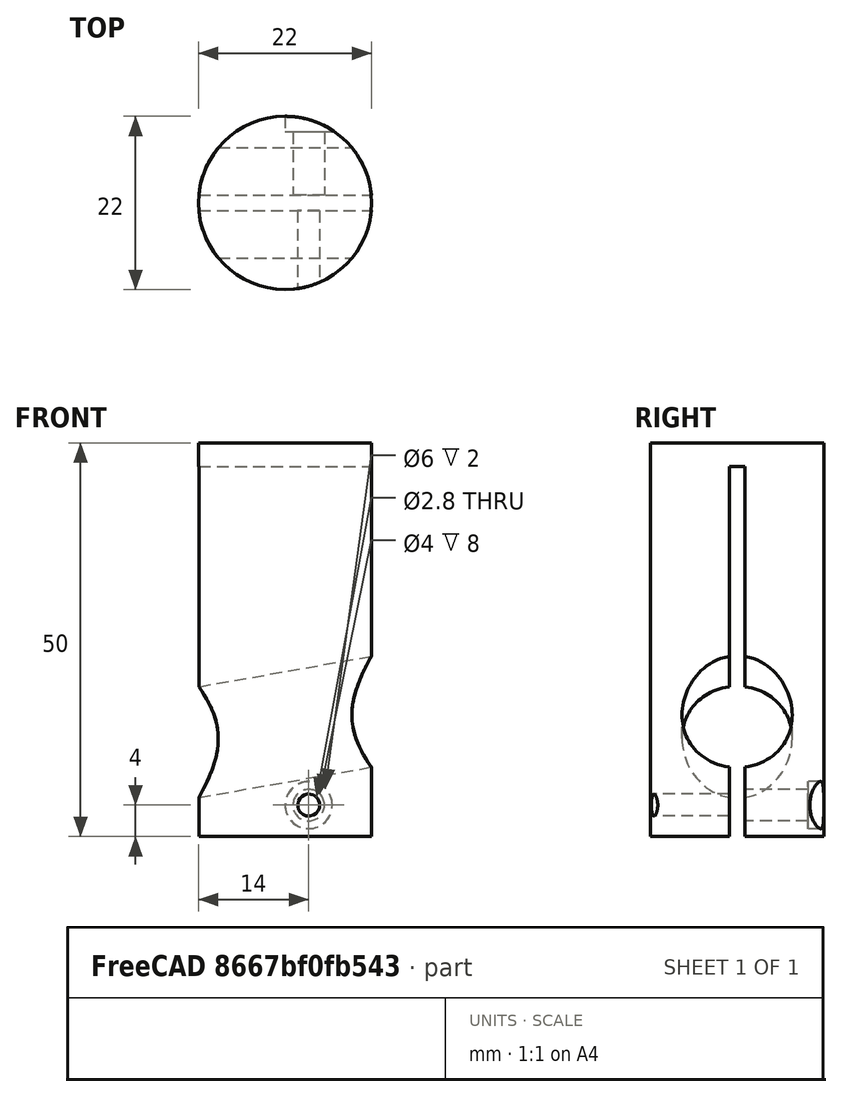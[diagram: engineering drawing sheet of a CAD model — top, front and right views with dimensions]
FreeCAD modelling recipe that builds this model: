
FCSTD DOCUMENT  (FreeCAD 0.19R)
Label: 14mmSSMount
License: All rights reserved
LicenseURL: http://en.wikipedia.org/wiki/All_rights_reserved
objects: Part::Cylinder×5, Part::Cut×5, PartDesign::Body×1, Part::Box×1
note: 12 computed .brp shape members not serialized (recipe doc carries the construction recipe); baked Part::Feature solids carry a one-line shape summary decoded from their .brp

FEATURE [PartDesign::Body] Body
  Origin = -> Origin
FEATURE [Part::Cylinder] Cylinder
  Angle = 360
  AttacherType = Attacher::AttachEngine3D
  Height = 50
  Radius = 11
FEATURE [Part::Cylinder] Cylinder001
  Angle = 360
  AttacherType = Attacher::AttachEngine3D
  Height = 100
  Placement = pos=(-28,0,9) rot=(0,1,0;1.39626rad)
  Radius = 7
FEATURE [Part::Cut] Cut
  Base = -> Cylinder
  Tool = -> Cylinder001
FEATURE [Part::Box] Box  label="Cube"
  AttacherType = Attacher::AttachEngine3D
  Height = 100
  Length = 100
  Placement = pos=(-17,-1,-53) rot=(0,0,1;0rad)
  Width = 2
FEATURE [Part::Cut] Cut001
  Base = -> Cut
  Tool = -> Box
FEATURE [Part::Cylinder] Cylinder002
  Angle = 360
  AttacherType = Attacher::AttachEngine3D
  Height = 28
  Placement = pos=(3,13,4) rot=(1,0,0;1.5708rad)
  Radius = 1.4
FEATURE [Part::Cylinder] Cylinder003
  Angle = 360
  AttacherType = Attacher::AttachEngine3D
  Height = 28
  Placement = pos=(3,28,4) rot=(1,0,0;1.5708rad)
  Radius = 2
FEATURE [Part::Cut] Cut002
  Base = -> Cut001
  Tool = -> Cylinder002
FEATURE [Part::Cut] Cut003
  Base = -> Cut002
  Tool = -> Cylinder003
FEATURE [Part::Cylinder] Cylinder004
  Angle = 360
  AttacherType = Attacher::AttachEngine3D
  Height = 28
  Placement = pos=(3,37,4) rot=(1,0,0;1.5708rad)
  Radius = 3
FEATURE [Part::Cut] Cut004
  Base = -> Cut003
  Tool = -> Cylinder004
